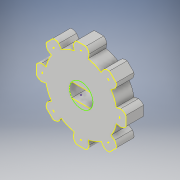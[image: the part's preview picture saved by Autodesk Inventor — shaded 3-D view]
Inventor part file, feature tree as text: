
AUTODESK INVENTOR PART (.ipt)
format: ipt  version: 2017 (Build 210142000, 142)  size: 207,872 bytes
history: native  units: in
note: dims shown in document units (in); Inventor stores cm internally (conversion verified against a paired STEP export)
features: sketch x4, extrude x2, pattern_circular x1, projected_geometry x1
ambient origin geometry x8: Origin, YZ Plane, XZ Plane, XY Plane, X Axis, Y Axis, Z Axis, Center Point
bodies: Solid1 (feature_tree)
feature tree (8):
  extrude  "Extrusion1"  Depth=0.15in TaperAngle=360.0deg
  pattern_circular  "Circular Pattern1"  [2 undecoded]
  extrude  "Extrusion3"  [1 undecoded]
  sketch  "Sketch4"  dims[d14=0.0591in]
  sketch  "Sketch5"  dims[d15=1.0in d16=0.0in]
  sketch  "Sketch1"  dims[d0=0.6in d1=360.0deg d2=0.04in d3=0.04in d4=0.075in d5=0.15in d6=0.0in d7=3.1496in d8=360.0deg]
  sketch  "Sketch3"  dims[d13=0.1969in]
  projected_geometry  "Projected Loop1"
note: 3 required parameter values undecoded (feature->parameter linkage not recoverable at this tier; creation-order binding heuristic only, values carry confidence <= 0.55)
